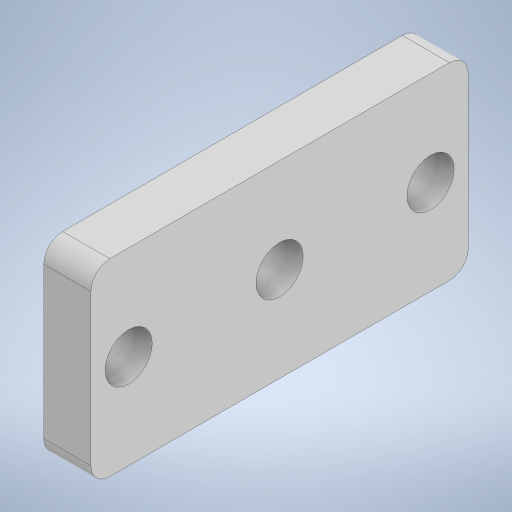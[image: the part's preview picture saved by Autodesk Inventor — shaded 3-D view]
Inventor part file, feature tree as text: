
AUTODESK INVENTOR PART (.ipt)
format: ipt  version: 2023 (Build 270158000, 158)  size: 213,504 bytes
history: native  units: mm
features: extrude x1, fillet x1, sketch x1
ambient origin geometry x8: Origin, YZ Plane, XZ Plane, XY Plane, X Axis, Y Axis, Z Axis, Center Point
bodies: Solido1 (feature_tree)
feature tree (3):
  extrude  "Estrusione1"  Depth=40.0mm
  fillet  "Raccordo1"  Radius=20.0mm
  sketch  "Schizzo1"
